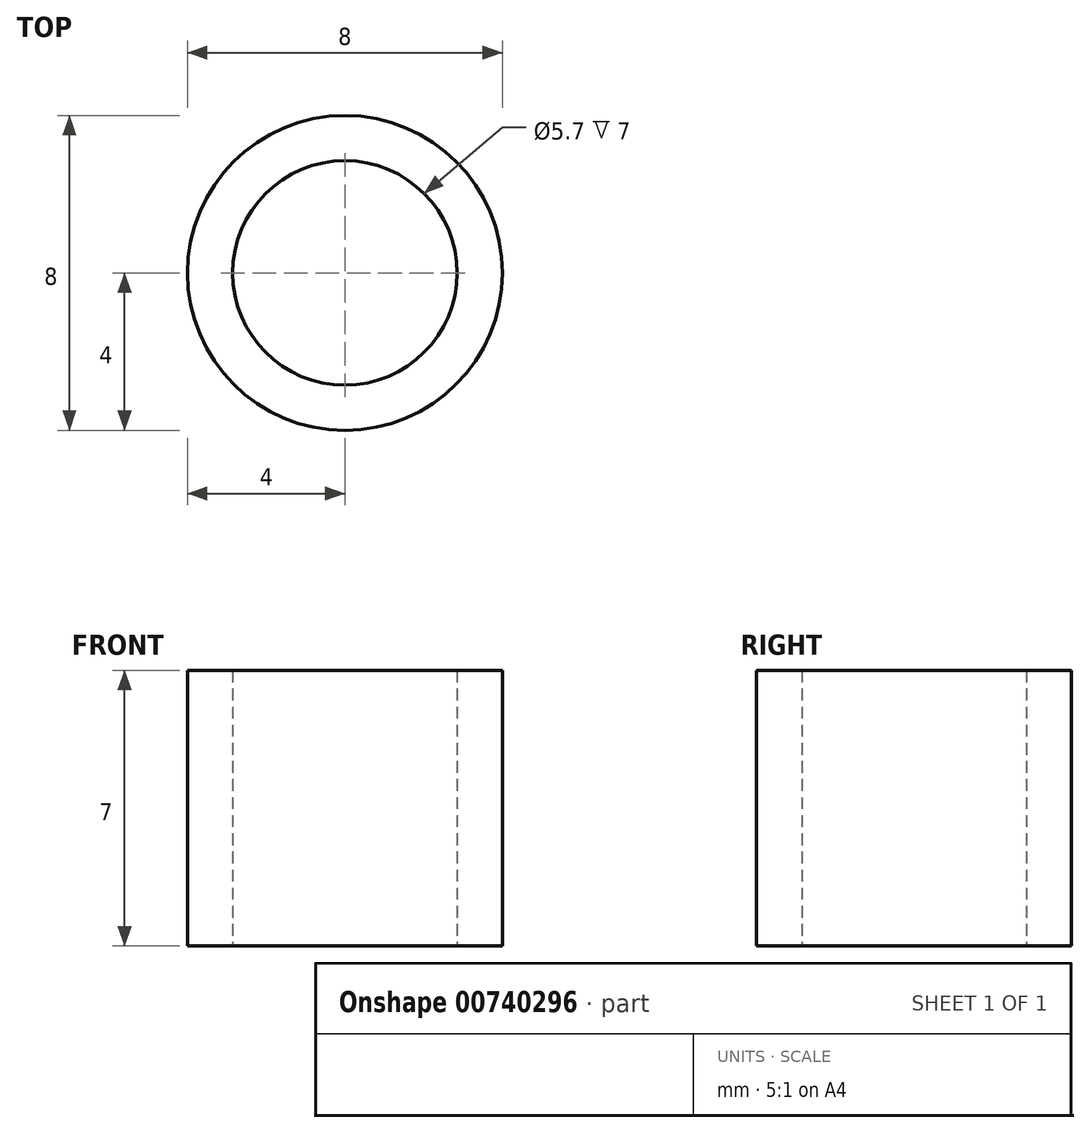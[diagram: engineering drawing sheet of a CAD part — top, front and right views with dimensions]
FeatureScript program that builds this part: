
annotation { "Feature Type Name" : "Feature", "Feature Type Description" : "" }
export const myFeature = defineFeature(function(context is Context, id is Id, definition is map)
    precondition{}
    {
        {
            var Q0;
            Q0=qCreatedBy(makeId("Top.planeOp"),FACE);
            var sketch = newSketch(context, id + "F0", { "sketchPlane" : qUnion([Q0])});
            skCircle(sketch, "E0", {"center": v(0, 0) * mm, "radius": 4 * mm});
            skCircle(sketch, "E1", {"center": v(0, 0) * mm, "radius": 2.85 * mm});
            skSolve(sketch);
        }
        {
            var Q0;
            Q0 = qSketchRegion(id + "F0", true);
            extrude(context, id + "F1", {"entities" : qUnion([Q0]), "depth" : 7 * mm, "offsetDistance" : 25 * mm});
        }
    });
